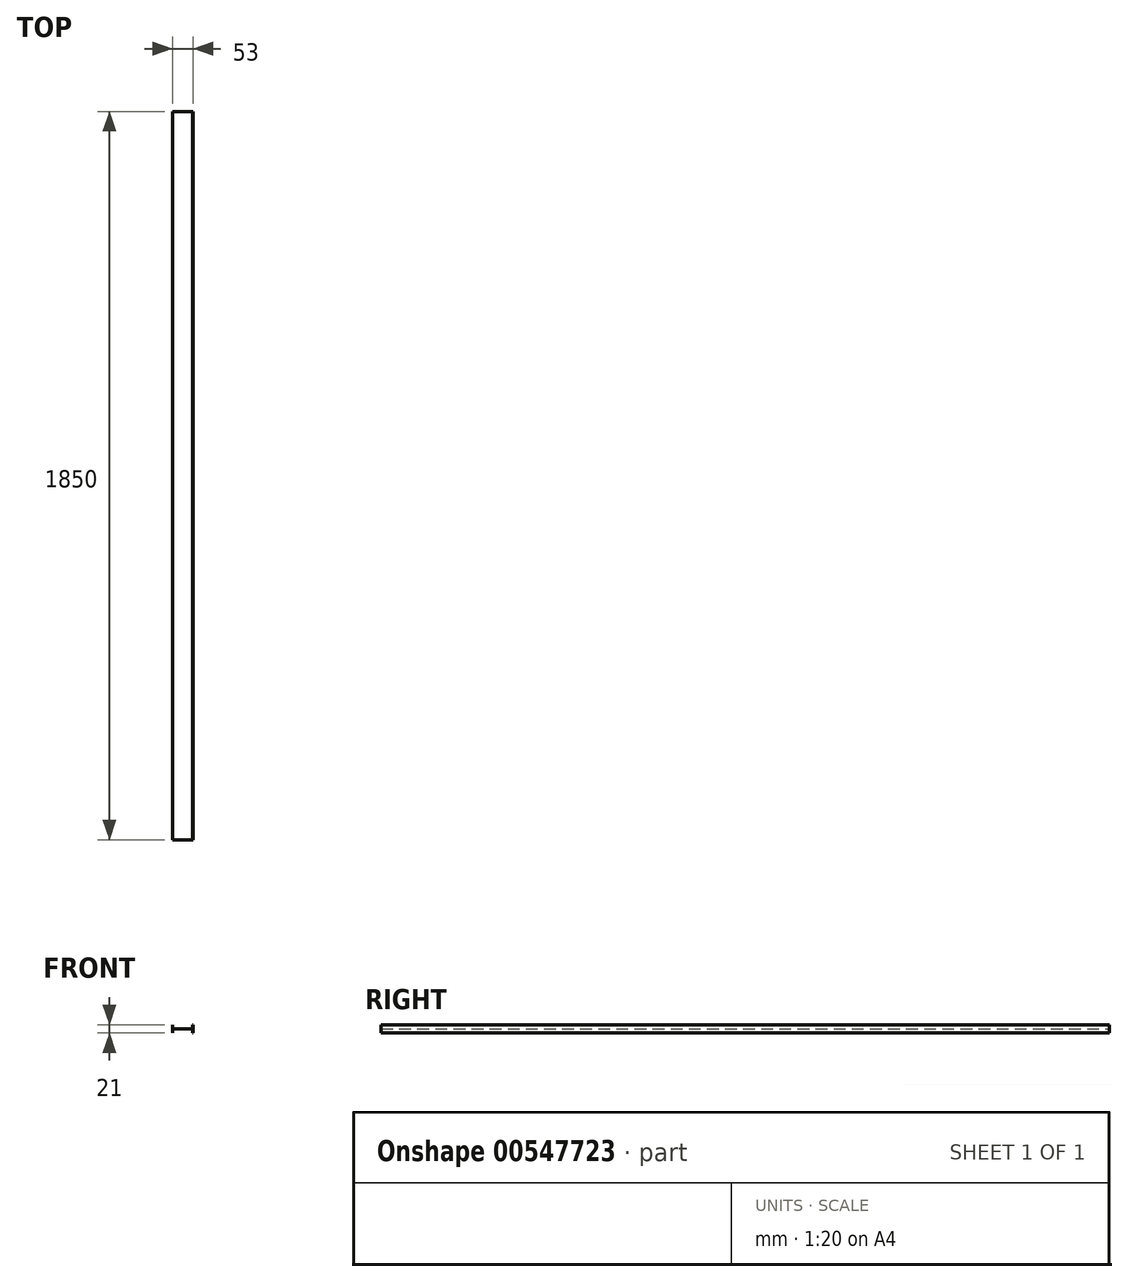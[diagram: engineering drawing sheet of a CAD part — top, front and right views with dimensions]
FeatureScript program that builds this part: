
annotation { "Feature Type Name" : "Feature", "Feature Type Description" : "" }
export const myFeature = defineFeature(function(context is Context, id is Id, definition is map)
    precondition{}
    {
        {
            var Q0;
            Q0=qCreatedBy(makeId("Front.planeOp"),FACE);
            var sketch = newSketch(context, id + "F0", { "sketchPlane" : qUnion([Q0])});
            skLineSegment(sketch, "E0", {"start": v(26.5, 10.5) * mm, "end": v(25.5, 10.5) * mm});
            skLineSegment(sketch, "E1", {"start": v(25.5, 10.5) * mm, "end": v(25.5, 0.5) * mm});
            skLineSegment(sketch, "E2", {"start": v(25.5, 0.5) * mm, "end": v(-25.5, 0.5) * mm});
            skLineSegment(sketch, "E3", {"start": v(-25.5, 0.5) * mm, "end": v(-25.5, 10.5) * mm});
            skLineSegment(sketch, "E4", {"start": v(-25.5, 10.5) * mm, "end": v(-26.5, 10.5) * mm});
            skLineSegment(sketch, "E5.MirrorCS", {"start": v(26.5, -10.5) * mm, "end": v(25.5, -10.5) * mm});
            skLineSegment(sketch, "E6.MirrorCS", {"start": v(-25.5, -10.5) * mm, "end": v(-26.5, -10.5) * mm});
            skLineSegment(sketch, "E7.MirrorCS", {"start": v(25.5, -10.5) * mm, "end": v(25.5, -0.5) * mm});
            skLineSegment(sketch, "E8.MirrorCS", {"start": v(25.5, -0.5) * mm, "end": v(-25.5, -0.5) * mm});
            skLineSegment(sketch, "E9.MirrorCS", {"start": v(-25.5, -0.5) * mm, "end": v(-25.5, -10.5) * mm});
            skLineSegment(sketch, "E10", {"start": v(-26.5, 10.5) * mm, "end": v(-26.5, -10.5) * mm});
            skLineSegment(sketch, "E11", {"start": v(26.5, 10.5) * mm, "end": v(26.5, -10.5) * mm});
            skSolve(sketch);
        }
        {
            var Q0;
            Q0 = qSketchRegion(id + "F0", true);
            extrude(context, id + "F1", {"entities" : qUnion([Q0]), "depth" : 1850 * mm, "offsetDistance" : 25 * mm});
        }
    });
